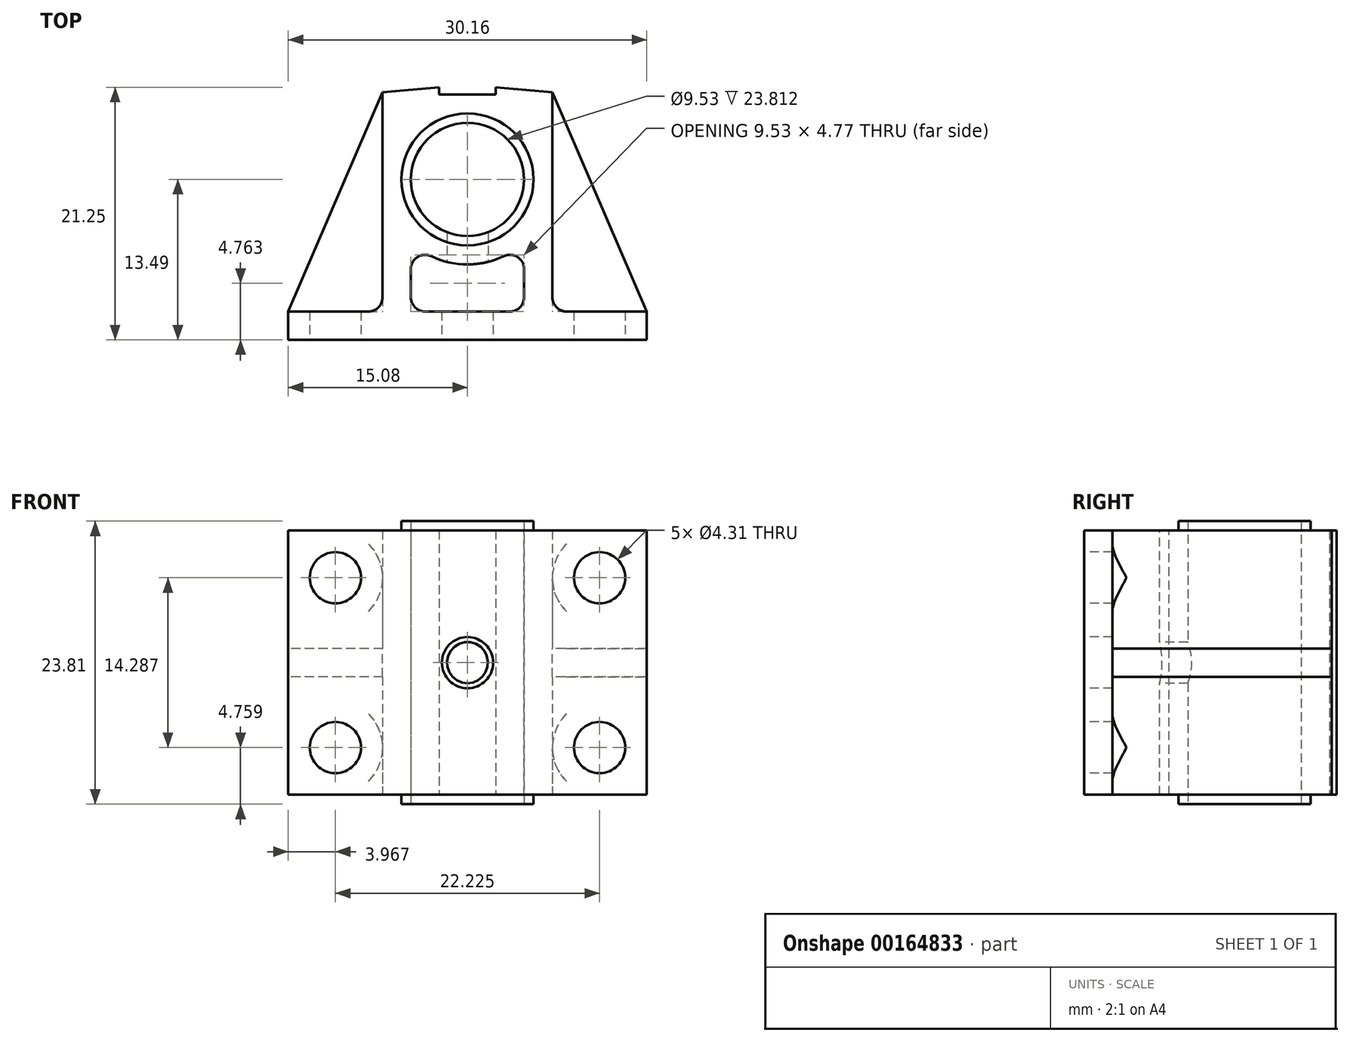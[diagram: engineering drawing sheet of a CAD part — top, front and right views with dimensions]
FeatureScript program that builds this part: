
annotation { "Feature Type Name" : "Feature", "Feature Type Description" : "" }
export const myFeature = defineFeature(function(context is Context, id is Id, definition is map)
    precondition{}
    {
        {
            var Q0;
            Q0=qCreatedBy(makeId("Top.planeOp"),FACE);
            var sketch = newSketch(context, id + "F0", { "sketchPlane" : qUnion([Q0])});
            skCircle(sketch, "E0", {"center": v(0, 0) * mm, "radius": 4.76 * mm});
            skLineSegment(sketch, "E1.top", {"start": v(15.08, -13.5) * mm, "end": v(-15.08, -13.5) * mm});
            skLineSegment(sketch, "E2", {"start": v(-15.08, -13.5) * mm, "end": v(-15.08, -11.11) * mm});
            skLineSegment(sketch, "E3", {"start": v(15.08, -13.5) * mm, "end": v(15.08, -11.11) * mm});
            skLineSegment(sketch, "E4", {"start": v(-15.08, -11.11) * mm, "end": v(-7.14, -11.11) * mm});
            skLineSegment(sketch, "E5", {"start": v(-7.14, -11.11) * mm, "end": v(-7.14, 7.34) * mm});
            skLineSegment(sketch, "E6", {"start": v(15.08, -11.11) * mm, "end": v(7.14, -11.11) * mm});
            skLineSegment(sketch, "E7", {"start": v(7.14, -11.11) * mm, "end": v(7.14, 7.34) * mm});
            skLineSegment(sketch, "E8", {"start": v(-7.14, -11.11) * mm, "end": v(7.14, -11.11) * mm, "construction": true});
            skLineSegment(sketch, "E9", {"start": v(0, -11.11) * mm, "end": v(0, -13.5) * mm, "construction": true});
            skLineSegment(sketch, "E10", {"start": v(0, 0) * mm, "end": v(0, -11.11) * mm, "construction": true});
            skLineSegment(sketch, "E11", {"start": v(0, 0) * mm, "end": v(0, 7.14) * mm, "construction": true});
            skLineSegment(sketch, "E12", {"start": v(-2.38, 7.14) * mm, "end": v(2.38, 7.14) * mm});
            skLineSegment(sketch, "E13", {"start": v(2.38, 7.14) * mm, "end": v(2.38, 7.76) * mm});
            skLineSegment(sketch, "E14", {"start": v(0, 0) * mm, "end": v(-7.14, 0) * mm, "construction": true});
            skLineSegment(sketch, "E15", {"start": v(2.38, 7.76) * mm, "end": v(7.14, 7.34) * mm});
            skLineSegment(sketch, "E16", {"start": v(-2.38, 7.14) * mm, "end": v(-2.38, 7.76) * mm});
            skLineSegment(sketch, "E17", {"start": v(-2.38, 7.76) * mm, "end": v(-7.14, 7.34) * mm});
            skLineSegment(sketch, "E18", {"start": v(0, 0) * mm, "end": v(0.7, 7.9) * mm, "construction": true});
            skLineSegment(sketch, "E19", {"start": v(0.7, 7.9) * mm, "end": v(2.38, 7.76) * mm, "construction": true});
            skLineSegment(sketch, "E20", {"start": v(7.14, 7.34) * mm, "end": v(127.2, -3.16) * mm, "construction": true});
            skLineSegment(sketch, "E21", {"start": v(15.08, -13.5) * mm, "end": v(254, -13.5) * mm, "construction": true});
            skSolve(sketch);
        }
        {
            var Q0;
            Q0=qSketchRegion(id+"F0",true);
            extrude(context, id + "F1", {"entities" : qUnion([Q0]), "depth" : 22.22 * mm});
        }
        {
            var Q0;
            Q0=makeQuery(id+"F1.opExtrude","CAP_FACE",FACE,{"disambiguationData":[OSD([sQuery(id+"F0.wireOp",EDGE,"oFMiMBZJ-tm7e-gSPN-Mg8Y-tAPpBSy2u1vv"),sQuery(id+"F0.wireOp",EDGE,"E0"),sQuery(id+"F0.wireOp",EDGE,"E1.top"),sQuery(id+"F0.wireOp",EDGE,"E1.left"),sQuery(id+"F0.wireOp",EDGE,"E1.right"),sQuery(id+"F0.wireOp",EDGE,"iWPHmNQj-lZC8-lhK7-cZkv-x0AVNYk73sRT"),sQuery(id+"F0.wireOp",EDGE,"Og7QZ6Jl-dYdA-JL6d-IRU5-9o3GzSJJQBdT"),sQuery(id+"F0.wireOp",EDGE,"E2"),sQuery(id+"F0.wireOp",EDGE,"E3"),sQuery(id+"F0.wireOp",EDGE,"E4"),sQuery(id+"F0.wireOp",EDGE,"E5"),sQuery(id+"F0.wireOp",EDGE,"E6"),sQuery(id+"F0.wireOp",EDGE,"E7")])],"isStart":true});
            cPlane(context, id + "F2", {"entities" : qUnion([Q0]), "cplaneType" : CPlaneType.OFFSET, "offset" : 11.1 * mm, "oppositeDirection" : true, "width" : 152.4 * mm, "height" : 152.4 * mm});
        }
        {
            var Q0;
            Q0=qCreatedBy(id+"F2.planeOp",FACE);
            var sketch = newSketch(context, id + "F3", { "sketchPlane" : qUnion([Q0])});
            skLineSegment(sketch, "E22", {"start": v(-7.14, -7.34) * mm, "end": v(-15.08, 11.11) * mm});
            skLineSegment(sketch, "E23", {"start": v(-7.14, 11.11) * mm, "end": v(-7.14, 11.11) * mm});
            skLineSegment(sketch, "E24", {"start": v(-7.14, 11.11) * mm, "end": v(-15.08, 11.11) * mm});
            skLineSegment(sketch, "E25", {"start": v(7.14, 11.11) * mm, "end": v(7.14, 11.11) * mm});
            skLineSegment(sketch, "E26", {"start": v(7.14, 11.11) * mm, "end": v(15.08, 11.11) * mm});
            skLineSegment(sketch, "E27", {"start": v(15.08, 11.11) * mm, "end": v(7.14, -7.34) * mm});
            skLineSegment(sketch, "E28", {"start": v(-7.14, -7.34) * mm, "end": v(-7.14, 11.11) * mm});
            skLineSegment(sketch, "E29", {"start": v(7.14, 11.11) * mm, "end": v(7.14, -7.34) * mm});
            skSolve(sketch);
        }
        {
            var Q0;
            Q0=qSketchRegion(id+"F3",true);
            extrude(context, id + "F4", {"entities" : qUnion([Q0]), "operationType" : NewBodyOperationType.ADD, "endBound" : BoundingType.SYMMETRIC, "depth" : 2.38 * mm});
        }
        {
            var Q0;
            Q0=makeQuery(id+"F1.opExtrude","CAP_FACE",FACE,{"disambiguationData":[OSD([sQuery(id+"F0.wireOp",EDGE,"oFMiMBZJ-tm7e-gSPN-Mg8Y-tAPpBSy2u1vv"),sQuery(id+"F0.wireOp",EDGE,"E0"),sQuery(id+"F0.wireOp",EDGE,"E1.top"),sQuery(id+"F0.wireOp",EDGE,"E1.left"),sQuery(id+"F0.wireOp",EDGE,"E1.right"),sQuery(id+"F0.wireOp",EDGE,"iWPHmNQj-lZC8-lhK7-cZkv-x0AVNYk73sRT"),sQuery(id+"F0.wireOp",EDGE,"Og7QZ6Jl-dYdA-JL6d-IRU5-9o3GzSJJQBdT"),sQuery(id+"F0.wireOp",EDGE,"E2"),sQuery(id+"F0.wireOp",EDGE,"E3"),sQuery(id+"F0.wireOp",EDGE,"E4"),sQuery(id+"F0.wireOp",EDGE,"E5"),sQuery(id+"F0.wireOp",EDGE,"E6"),sQuery(id+"F0.wireOp",EDGE,"E7")])],"isStart":true});
            var sketch = newSketch(context, id + "F5", { "sketchPlane" : qUnion([Q0])});
            skCircle(sketch, "E30", {"center": v(0, 0) * mm, "radius": 4.76 * mm});
            skCircle(sketch, "E31", {"center": v(0, 0) * mm, "radius": 5.56 * mm});
            skSolve(sketch);
        }
        {
            var Q0;
            Q0=makeQuery(id+"F1.opExtrude","CAP_FACE",FACE,{"disambiguationData":[OSD([sQuery(id+"F0.wireOp",EDGE,"oFMiMBZJ-tm7e-gSPN-Mg8Y-tAPpBSy2u1vv"),sQuery(id+"F0.wireOp",EDGE,"E0"),sQuery(id+"F0.wireOp",EDGE,"E1.top"),sQuery(id+"F0.wireOp",EDGE,"E1.left"),sQuery(id+"F0.wireOp",EDGE,"E1.right"),sQuery(id+"F0.wireOp",EDGE,"iWPHmNQj-lZC8-lhK7-cZkv-x0AVNYk73sRT"),sQuery(id+"F0.wireOp",EDGE,"Og7QZ6Jl-dYdA-JL6d-IRU5-9o3GzSJJQBdT"),sQuery(id+"F0.wireOp",EDGE,"E2"),sQuery(id+"F0.wireOp",EDGE,"E3"),sQuery(id+"F0.wireOp",EDGE,"E4"),sQuery(id+"F0.wireOp",EDGE,"E5"),sQuery(id+"F0.wireOp",EDGE,"E6"),sQuery(id+"F0.wireOp",EDGE,"E7")])],"isStart":false});
            cPlane(context, id + "F6", {"entities" : qUnion([Q0]), "cplaneType" : CPlaneType.OFFSET, "offset" : 0.8 * mm, "width" : 152.4 * mm, "height" : 152.4 * mm});
        }
        {
            var Q0;
            Q0=qSketchRegion(id+"F5",true);
            var Q1;
            Q1=qCreatedBy(id+"F6.planeOp",FACE);
            extrude(context, id + "F7", {"entities" : qUnion([Q0]), "operationType" : NewBodyOperationType.ADD, "depth" : 0.8 * mm, "hasSecondDirection" : true, "secondDirectionBound" : SecondDirectionBoundingType.UP_TO_SURFACE, "secondDirectionOppositeDirection" : true, "secondDirectionBoundEntityFace" : qUnion([Q1]), "secondDirectionDepth" : 25.4 * mm});
        }
        {
            var Q0;
            Q0=makeQuery(id+"F1.opExtrude","SWEPT_FACE",FACE,{"disambiguationData":[OSD([sQuery(id+"F0.wireOp",EDGE,"E1.top")])]});
            var sketch = newSketch(context, id + "F8", { "sketchPlane" : qUnion([Q0])});
            skLineSegment(sketch, "E32", {"start": v(0, 22.23) * mm, "end": v(0, 0) * mm, "construction": true});
            skCircle(sketch, "E33", {"center": v(0, 11.11) * mm, "radius": 1.73 * mm});
            skSolve(sketch);
        }
        {
            var Q0;
            Q0=qSketchRegion(id+"F8",true);
            var Q1;
            Q1=makeQuery(id+"F7.boolean.opBoolean","MERGE",FACE,{"derivedFrom":[makeQuery(id+"F1.opExtrude","SWEPT_FACE",FACE,{"disambiguationData":[OSD([sQuery(id+"F0.wireOp",EDGE,"E0")])]}),makeQuery(id+"F7.opExtrude","SWEPT_FACE",FACE,{"disambiguationData":[OSD([sQuery(id+"F5.wireOp",EDGE,"E30")])]})]});
            extrude(context, id + "F9", {"entities" : qUnion([Q0]), "operationType" : NewBodyOperationType.REMOVE, "endBound" : BoundingType.UP_TO_SURFACE, "oppositeDirection" : true, "endBoundEntityFace" : qUnion([Q1]), "depth" : 25.4 * mm});
        }
        {
            var Q0;
            Q0=makeQuery(id+"F1.opExtrude","CAP_FACE",FACE,{"disambiguationData":[OSD([sQuery(id+"F0.wireOp",EDGE,"oFMiMBZJ-tm7e-gSPN-Mg8Y-tAPpBSy2u1vv"),sQuery(id+"F0.wireOp",EDGE,"E0"),sQuery(id+"F0.wireOp",EDGE,"E1.top"),sQuery(id+"F0.wireOp",EDGE,"E1.left"),sQuery(id+"F0.wireOp",EDGE,"E1.right"),sQuery(id+"F0.wireOp",EDGE,"iWPHmNQj-lZC8-lhK7-cZkv-x0AVNYk73sRT"),sQuery(id+"F0.wireOp",EDGE,"Og7QZ6Jl-dYdA-JL6d-IRU5-9o3GzSJJQBdT"),sQuery(id+"F0.wireOp",EDGE,"E2"),sQuery(id+"F0.wireOp",EDGE,"E3"),sQuery(id+"F0.wireOp",EDGE,"E4"),sQuery(id+"F0.wireOp",EDGE,"E5"),sQuery(id+"F0.wireOp",EDGE,"E6"),sQuery(id+"F0.wireOp",EDGE,"E7")])],"isStart":false});
            var sketch = newSketch(context, id + "F10", { "sketchPlane" : qUnion([Q0])});
            skLineSegment(sketch, "E34.bottom", {"start": v(-4.76, -11.11) * mm, "end": v(4.76, -11.11) * mm});
            skLineSegment(sketch, "E34.top", {"start": v(-4.76, -5.32) * mm, "end": v(4.76, -5.32) * mm, "construction": true});
            skLineSegment(sketch, "E34.left", {"start": v(-4.76, -11.11) * mm, "end": v(-4.76, -5.32) * mm});
            skLineSegment(sketch, "E34.right", {"start": v(4.76, -11.11) * mm, "end": v(4.76, -5.32) * mm});
            skLineSegment(sketch, "E35", {"start": v(0, -11.11) * mm, "end": v(0, -13.5) * mm, "construction": true});
            skLineSegment(sketch, "E36", {"start": v(4.76, -11.11) * mm, "end": v(7.14, -11.11) * mm, "construction": true});
            skArc(sketch, "E37", {"start": v(-4.76, -5.32) * mm, "mid": v(0, -7.14) * mm, "end": v(4.76, -5.32) * mm});
            skSolve(sketch);
        }
        {
            var Q0;
            Q0=qSketchRegion(id+"F10",true);
            var Q1;
            Q1=makeQuery(id+"F1.opExtrude","CAP_FACE",FACE,{"disambiguationData":[OSD([sQuery(id+"F0.wireOp",EDGE,"oFMiMBZJ-tm7e-gSPN-Mg8Y-tAPpBSy2u1vv"),sQuery(id+"F0.wireOp",EDGE,"E0"),sQuery(id+"F0.wireOp",EDGE,"E1.top"),sQuery(id+"F0.wireOp",EDGE,"E1.left"),sQuery(id+"F0.wireOp",EDGE,"E1.right"),sQuery(id+"F0.wireOp",EDGE,"iWPHmNQj-lZC8-lhK7-cZkv-x0AVNYk73sRT"),sQuery(id+"F0.wireOp",EDGE,"Og7QZ6Jl-dYdA-JL6d-IRU5-9o3GzSJJQBdT"),sQuery(id+"F0.wireOp",EDGE,"E2"),sQuery(id+"F0.wireOp",EDGE,"E3"),sQuery(id+"F0.wireOp",EDGE,"E4"),sQuery(id+"F0.wireOp",EDGE,"E5"),sQuery(id+"F0.wireOp",EDGE,"E6"),sQuery(id+"F0.wireOp",EDGE,"E7")])],"isStart":true});
            extrude(context, id + "F11", {"entities" : qUnion([Q0]), "operationType" : NewBodyOperationType.REMOVE, "endBound" : BoundingType.UP_TO_SURFACE, "oppositeDirection" : true, "endBoundEntityFace" : qUnion([Q1]), "depth" : 25.4 * mm});
        }
        {
            var Q0;
            Q0=makeQuery(id+"F1.opExtrude","SWEPT_FACE",FACE,{"disambiguationData":[OSD([sQuery(id+"F0.wireOp",EDGE,"E1.top")])]});
            var sketch = newSketch(context, id + "F12", { "sketchPlane" : qUnion([Q0])});
            skCircle(sketch, "E38", {"center": v(0, 11.11) * mm, "radius": 2.15 * mm});
            skSolve(sketch);
        }
        {
            var Q0;
            Q0=qSketchRegion(id+"F12",true);
            var Q1;
            Q1=makeQuery(id+"F11.boolean.opBoolean","COPY",FACE,{"derivedFrom":makeQuery(id+"F11.opExtrude","SWEPT_FACE",FACE,{"disambiguationData":[OSD([sQuery(id+"F10.wireOp",EDGE,"E34.bottom")])]})});
            extrude(context, id + "F13", {"entities" : qUnion([Q0]), "operationType" : NewBodyOperationType.REMOVE, "endBound" : BoundingType.UP_TO_SURFACE, "oppositeDirection" : true, "endBoundEntityFace" : qUnion([Q1]), "depth" : 25.4 * mm});
        }
        {
            var Q0;
            {var subQ0=sQuery(id+"F0.wireOp",EDGE,"E7");var subQ1=sQuery(id+"F0.wireOp",EDGE,"E6");Q0=makeQuery(id+"F4.boolean.opBoolean","SPLIT",EDGE,{"disambiguationData":[TD([makeQuery(id+"F4.opExtrude","CAP_FACE",FACE,{"disambiguationData":[OSD([sQuery(id+"F3.wireOp",EDGE,"kuT9Lr5W-Ujlv-qyoe-8bON-kbdIo9kqYZIf"),sQuery(id+"F3.wireOp",EDGE,"E25"),sQuery(id+"F3.wireOp",EDGE,"E26"),sQuery(id+"F3.wireOp",EDGE,"E27")])],"isStart":true})])],"derivedFrom":makeQuery(id+"F1.opExtrude","SWEPT_EDGE",EDGE,{"disambiguationData":[OSD([subQ1,subQ0])]})});}
            var Q1;
            {var subQ0=sQuery(id+"F0.wireOp",EDGE,"E7");var subQ1=sQuery(id+"F0.wireOp",EDGE,"E6");Q1=makeQuery(id+"F4.boolean.opBoolean","SPLIT",EDGE,{"disambiguationData":[TD([makeQuery(id+"F4.opExtrude","CAP_FACE",FACE,{"disambiguationData":[OSD([sQuery(id+"F3.wireOp",EDGE,"kuT9Lr5W-Ujlv-qyoe-8bON-kbdIo9kqYZIf"),sQuery(id+"F3.wireOp",EDGE,"E25"),sQuery(id+"F3.wireOp",EDGE,"E26"),sQuery(id+"F3.wireOp",EDGE,"E27")])],"isStart":false})])],"derivedFrom":makeQuery(id+"F1.opExtrude","SWEPT_EDGE",EDGE,{"disambiguationData":[OSD([subQ1,subQ0])]})});}
            var Q2;
            {var subQ0=sQuery(id+"F0.wireOp",EDGE,"E5");var subQ1=sQuery(id+"F0.wireOp",EDGE,"E4");Q2=makeQuery(id+"F4.boolean.opBoolean","SPLIT",EDGE,{"disambiguationData":[TD([makeQuery(id+"F4.opExtrude","CAP_FACE",FACE,{"disambiguationData":[OSD([sQuery(id+"F3.wireOp",EDGE,"E22"),sQuery(id+"F3.wireOp",EDGE,"yiKBqqz0-a8bt-GbF6-MsWU-omjT0H6QG2cN"),sQuery(id+"F3.wireOp",EDGE,"E23"),sQuery(id+"F3.wireOp",EDGE,"E24")])],"isStart":true})])],"derivedFrom":makeQuery(id+"F1.opExtrude","SWEPT_EDGE",EDGE,{"disambiguationData":[OSD([subQ1,subQ0])]})});}
            var Q3;
            {var subQ0=sQuery(id+"F0.wireOp",EDGE,"E5");var subQ1=sQuery(id+"F0.wireOp",EDGE,"E4");Q3=makeQuery(id+"F4.boolean.opBoolean","SPLIT",EDGE,{"disambiguationData":[TD([makeQuery(id+"F4.opExtrude","CAP_FACE",FACE,{"disambiguationData":[OSD([sQuery(id+"F3.wireOp",EDGE,"E22"),sQuery(id+"F3.wireOp",EDGE,"yiKBqqz0-a8bt-GbF6-MsWU-omjT0H6QG2cN"),sQuery(id+"F3.wireOp",EDGE,"E23"),sQuery(id+"F3.wireOp",EDGE,"E24")])],"isStart":false})])],"derivedFrom":makeQuery(id+"F1.opExtrude","SWEPT_EDGE",EDGE,{"disambiguationData":[OSD([subQ1,subQ0])]})});}
            var Q4;
            Q4=makeQuery(id+"F11.boolean.opBoolean","COPY",EDGE,{"derivedFrom":makeQuery(id+"F11.opExtrude","SWEPT_EDGE",EDGE,{"disambiguationData":[OSD([sQuery(id+"F10.wireOp",EDGE,"E34.bottom"),sQuery(id+"F10.wireOp",EDGE,"E34.left")])]})});
            var Q5;
            Q5=makeQuery(id+"F11.boolean.opBoolean","COPY",EDGE,{"derivedFrom":makeQuery(id+"F11.opExtrude","SWEPT_EDGE",EDGE,{"disambiguationData":[OSD([sQuery(id+"F10.wireOp",EDGE,"E34.bottom"),sQuery(id+"F10.wireOp",EDGE,"E34.right")])]})});
            var Q6;
            Q6=makeQuery(id+"F11.boolean.opBoolean","COPY",EDGE,{"derivedFrom":makeQuery(id+"F11.opExtrude","SWEPT_EDGE",EDGE,{"disambiguationData":[OSD([sQuery(id+"F10.wireOp",EDGE,"E34.right"),sQuery(id+"F10.wireOp",EDGE,"E37")])]})});
            var Q7;
            Q7=makeQuery(id+"F11.boolean.opBoolean","COPY",EDGE,{"derivedFrom":makeQuery(id+"F11.opExtrude","SWEPT_EDGE",EDGE,{"disambiguationData":[OSD([sQuery(id+"F10.wireOp",EDGE,"E34.left"),sQuery(id+"F10.wireOp",EDGE,"E37")])]})});
            fillet(context, id + "F14", {"entities" : qUnion([Q0, Q1, Q2, Q3, Q4, Q5, Q6, Q7]), "radius" : 1.2 * mm, "tangentPropagation" : true, "allowEdgeOverflow" : false});
        }
        {
            var Q0;
            Q0=makeQuery(id+"F1.opExtrude","SWEPT_FACE",FACE,{"disambiguationData":[OSD([sQuery(id+"F0.wireOp",EDGE,"E1.top")])]});
            var sketch = newSketch(context, id + "F15", { "sketchPlane" : qUnion([Q0])});
            skLineSegment(sketch, "E39.bottom", {"start": v(11.11, 18.26) * mm, "end": v(-11.11, 18.26) * mm, "construction": true});
            skLineSegment(sketch, "E39.top", {"start": v(11.11, 3.97) * mm, "end": v(-11.11, 3.97) * mm, "construction": true});
            skLineSegment(sketch, "E39.left", {"start": v(11.11, 18.26) * mm, "end": v(11.11, 3.97) * mm, "construction": true});
            skLineSegment(sketch, "E39.right", {"start": v(-11.11, 18.26) * mm, "end": v(-11.11, 3.97) * mm, "construction": true});
            skPoint(sketch, "E39.middle", {"position": v(0, 11.11) * mm});
            skLineSegment(sketch, "E40.bottom", {"start": v(11.11, 18.26) * mm, "end": v(15.08, 18.26) * mm, "construction": true});
            skLineSegment(sketch, "E40.top", {"start": v(11.11, 22.23) * mm, "end": v(15.08, 22.23) * mm, "construction": true});
            skLineSegment(sketch, "E40.left", {"start": v(11.11, 18.26) * mm, "end": v(11.11, 22.23) * mm, "construction": true});
            skLineSegment(sketch, "E40.right", {"start": v(15.08, 18.26) * mm, "end": v(15.08, 22.23) * mm, "construction": true});
            skCircle(sketch, "E41", {"center": v(11.11, 18.26) * mm, "radius": 2.15 * mm});
            skCircle(sketch, "E42", {"center": v(-11.11, 18.26) * mm, "radius": 2.15 * mm});
            skCircle(sketch, "E43", {"center": v(-11.11, 3.97) * mm, "radius": 2.15 * mm});
            skCircle(sketch, "E44", {"center": v(11.11, 3.97) * mm, "radius": 2.15 * mm});
            skSolve(sketch);
        }
        {
            var Q0;
            Q0 = qSketchRegion(id + "F15", true);
            var Q1;
            {var subQ0=sQuery(id+"F3.wireOp",EDGE,"E27");var subQ3=sQuery(id+"F0.wireOp",EDGE,"E6");Q1=makeQuery(id+"F4.boolean.opBoolean","SPLIT",FACE,{"disambiguationData":[TD([makeQuery(id+"F4.opExtrude","CAP_FACE",FACE,{"disambiguationData":[OSD([sQuery(id+"F3.wireOp",EDGE,"E26"),subQ0,sQuery(id+"F3.wireOp",EDGE,"E29")])],"isStart":true})])],"derivedFrom":makeQuery(id+"F1.opExtrude","SWEPT_FACE",FACE,{"disambiguationData":[OSD([subQ3])]})});}
            extrude(context, id + "F16", {"entities" : qUnion([Q0]), "operationType" : NewBodyOperationType.REMOVE, "endBound" : BoundingType.UP_TO_SURFACE, "oppositeDirection" : true, "endBoundEntityFace" : qUnion([Q1]), "depth" : 25.4 * mm});
        }
        {
            var Q0;
            {var subQ0=sQuery(id+"F3.wireOp",EDGE,"E27");var subQ3=sQuery(id+"F0.wireOp",EDGE,"E6");Q0=makeQuery(id+"F4.boolean.opBoolean","SPLIT",FACE,{"disambiguationData":[TD([makeQuery(id+"F4.opExtrude","CAP_FACE",FACE,{"disambiguationData":[OSD([sQuery(id+"F3.wireOp",EDGE,"E26"),subQ0,sQuery(id+"F3.wireOp",EDGE,"E29")])],"isStart":true})])],"derivedFrom":makeQuery(id+"F1.opExtrude","SWEPT_FACE",FACE,{"disambiguationData":[OSD([subQ3])]})});}
            var sketch = newSketch(context, id + "F17", { "sketchPlane" : qUnion([Q0])});
            skCircle(sketch, "E45", {"center": v(11.11, 18.26) * mm, "radius": 3.97 * mm});
            skCircle(sketch, "E46", {"center": v(11.11, 3.97) * mm, "radius": 3.97 * mm});
            skCircle(sketch, "E47", {"center": v(-11.11, 3.97) * mm, "radius": 3.97 * mm});
            skCircle(sketch, "E48", {"center": v(-11.11, 18.26) * mm, "radius": 3.97 * mm});
            skSolve(sketch);
        }
        {
            var Q0;
            Q0 = qSketchRegion(id + "F17", true);
            var Q1;
            {var subQ0=sQuery(id+"F0.wireOp",EDGE,"E5");var subQ1=sQuery(id+"F0.wireOp",EDGE,"E4");Q1=makeQuery(id+"F14.opFillet","BLEND_FACE",FACE,{"disambiguationData":[OSD([subQ1,subQ0]),TDD([makeQuery(id+"F4.boolean.opBoolean","SPLIT",EDGE,{"disambiguationData":[TD([makeQuery(id+"F4.opExtrude","CAP_FACE",FACE,{"disambiguationData":[OSD([sQuery(id+"F3.wireOp",EDGE,"E22"),sQuery(id+"F3.wireOp",EDGE,"E24"),sQuery(id+"F3.wireOp",EDGE,"E28")])],"isStart":true})])],"derivedFrom":makeQuery(id+"F1.opExtrude","SWEPT_EDGE",EDGE,{"disambiguationData":[OSD([subQ1,subQ0])]})})])]});}
            extrude(context, id + "F18", {"entities" : qUnion([Q0]), "operationType" : NewBodyOperationType.REMOVE, "endBound" : BoundingType.THROUGH_ALL, "endBoundEntityFace" : qUnion([Q1]), "depth" : 25.4 * mm});
        }
    });
